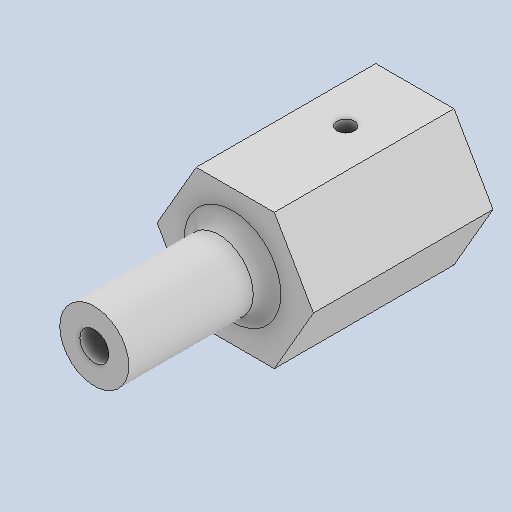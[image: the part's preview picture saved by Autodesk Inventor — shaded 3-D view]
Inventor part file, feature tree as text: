
AUTODESK INVENTOR PART (.ipt)
format: ipt  version: 2022 (Build 260153000, 153)  size: 156,672 bytes
history: native  units: mm
features: reference x12, extrude x4, sketch x4, other x3, fillet x1, projected_geometry x1
ambient origin geometry x8: Origin, YZ Plane, XZ Plane, XY Plane, X Axis, Y Axis, Z Axis, Center Point
bodies: Solid1 (feature_tree)
feature tree (25):
  extrude  "Extrusion1"  Depth=3.0mm TaperAngle=0.0deg
  extrude  "Extrusion2"  Depth=2.1mm
  extrude  "Extrusion3"  Depth=1.0mm
  fillet  "Fillet1"  Radius=1.25mm
  extrude  "Extrusion4"  [1 undecoded]
  sketch  "Sketch1"  dims[d0=10.0mm d1=0.0mm d2=3.0mm d3=0.0mm]
  reference  "Reference1"
  reference  "Reference2"
  reference  "Reference3"
  reference  "Reference4"
  reference  "Reference5"
  reference  "Reference6"
  reference  "Reference7"
  reference  "Reference8"
  reference  "Reference9"
  reference  "Reference10"
  reference  "Reference11"
  reference  "Reference12"
  sketch  "Sketch2"  dims[d4=5.0mm d5=2.1mm]
  sketch  "Sketch3"  dims[d6=10.0mm d7=0.0mm d8=1.0mm d9=1.25mm]
  sketch  "Sketch4"  dims[d10=10.0mm d11=0.0mm]
  projected_geometry  "Projected Loop1"
  other  "Caja_Reductora.iam"
  other  "Rodamiento_Ejes:5"
  other  "Hombro_Ejes:10"
note: 1 required parameter value undecoded (feature->parameter linkage not recoverable at this tier; creation-order binding heuristic only, values carry confidence <= 0.55)
